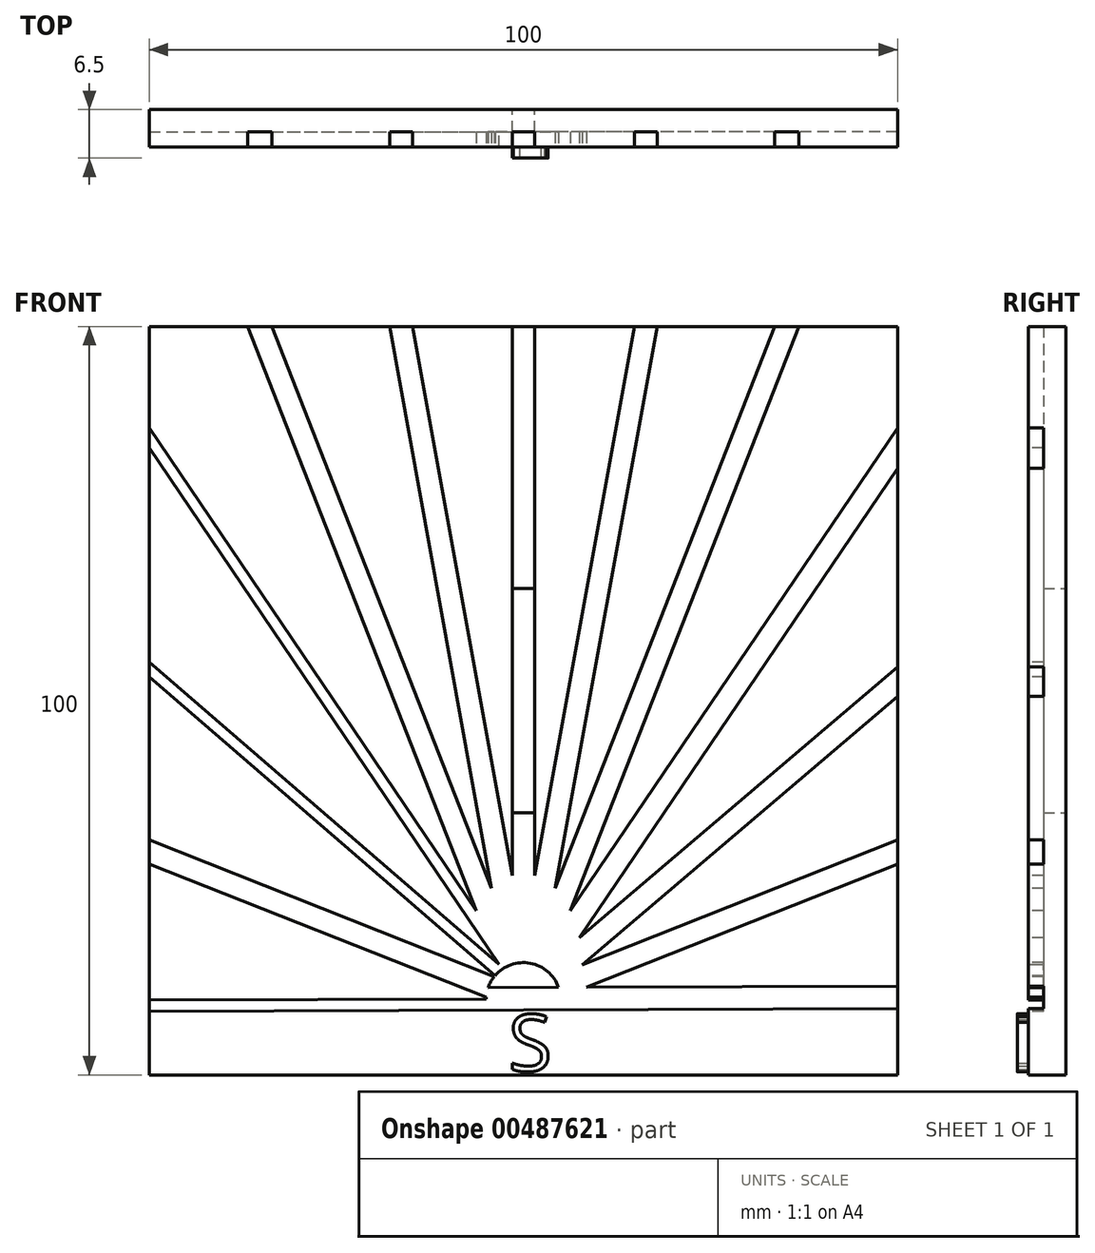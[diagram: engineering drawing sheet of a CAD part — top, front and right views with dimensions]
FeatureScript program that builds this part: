
annotation { "Feature Type Name" : "Feature", "Feature Type Description" : "" }
export const myFeature = defineFeature(function(context is Context, id is Id, definition is map)
    precondition{}
    {
        {
            var Q0;
            Q0=qCreatedBy(makeId("Front.planeOp"),FACE);
            var sketch = newSketch(context, id + "F0", { "sketchPlane" : qUnion([Q0])});
            skLineSegment(sketch, "E0.bottom", {"start": v(50, -50) * mm, "end": v(-50, -50) * mm});
            skLineSegment(sketch, "E0.top", {"start": v(50, 50) * mm, "end": v(-50, 50) * mm});
            skLineSegment(sketch, "E0.left", {"start": v(50, -50) * mm, "end": v(50, 50) * mm});
            skLineSegment(sketch, "E0.right", {"start": v(-50, -50) * mm, "end": v(-50, 50) * mm});
            skPoint(sketch, "E0.middle", {"position": v(0, 0) * mm});
            skLineSegment(sketch, "E1.bottom", {"start": v(1.5, -15) * mm, "end": v(-1.5, -15) * mm});
            skLineSegment(sketch, "E1.top", {"start": v(1.5, 15) * mm, "end": v(-1.5, 15) * mm});
            skLineSegment(sketch, "E1.left", {"start": v(1.5, -15) * mm, "end": v(1.5, 15) * mm});
            skLineSegment(sketch, "E1.right", {"start": v(-1.5, -15) * mm, "end": v(-1.5, 15) * mm});
            skSolve(sketch);
        }
        {
            var Q0;
            Q0=makeQuery(id+"F0.imprint","IMPRINT",FACE,{"disambiguationData":[TD([[makeQuery(id+"F0.imprint","IMPRINT",EDGE,{"derivedFrom":sQuery(id+"F0.wireOp",EDGE,"E0.bottom")}),-1.0]])]});
            extrude(context, id + "F1", {"entities" : qUnion([Q0]), "depth" : 5 * mm});
        }
        {
            var Q0;
            Q0=makeQuery(id+"F1.opExtrude","CAP_FACE",FACE,{"disambiguationData":[OSD([sQuery(id+"F0.wireOp",EDGE,"E0.bottom"),sQuery(id+"F0.wireOp",EDGE,"E0.top"),sQuery(id+"F0.wireOp",EDGE,"E0.left"),sQuery(id+"F0.wireOp",EDGE,"E0.right"),sQuery(id+"F0.wireOp",EDGE,"E1.bottom"),sQuery(id+"F0.wireOp",EDGE,"E1.top"),sQuery(id+"F0.wireOp",EDGE,"E1.left"),sQuery(id+"F0.wireOp",EDGE,"E1.right")])],"isStart":false});
            var sketch = newSketch(context, id + "F2", { "sketchPlane" : qUnion([Q0])});
            skPoint(sketch, "E2", {"position": v(0, -40) * mm});
            skLineSegment(sketch, "E3", {"start": v(-50, -40) * mm, "end": v(50, -40) * mm});
            skPoint(sketch, "E4", {"position": v(-50, -20.23) * mm});
            skLineSegment(sketch, "E5", {"start": v(0, -40) * mm, "end": v(-50, -20.23) * mm});
            skCircle(sketch, "E6", {"center": v(0, -40) * mm, "radius": 5 * mm});
            skPoint(sketch, "E7", {"position": v(-50, -18.62) * mm});
            skPoint(sketch, "E8", {"position": v(-50, -21.85) * mm});
            skLineSegment(sketch, "E9", {"start": v(-50, -21.85) * mm, "end": v(-4.99, -39.64) * mm});
            skLineSegment(sketch, "E10", {"start": v(-50, -18.62) * mm, "end": v(-3.88, -36.85) * mm});
            skSolve(sketch);
        }
        {
            var Q0;
            {var subQ5=sQuery(id+"F2.wireOp",EDGE,"E10");Q0=makeQuery(id+"F2.imprint","IMPRINT",FACE,{"disambiguationData":[TD([[makeQuery(id+"F2.imprint","IMPRINT",EDGE,{"derivedFrom":subQ5}),-1.0]])]});}
            var Q1;
            {var subQ5=sQuery(id+"F2.wireOp",EDGE,"E9");Q1=makeQuery(id+"F2.imprint","IMPRINT",FACE,{"disambiguationData":[TD([[makeQuery(id+"F2.imprint","IMPRINT",EDGE,{"derivedFrom":subQ5}),1.0]])]});}
            extrude(context, id + "F3", {"entities" : qUnion([Q0, Q1]), "operationType" : NewBodyOperationType.REMOVE, "oppositeDirection" : true, "depth" : 2 * mm});
        }
        {
            var Q0;
            Q0=makeQuery(id+"F1.opExtrude","CAP_FACE",FACE,{"disambiguationData":[OSD([sQuery(id+"F0.wireOp",EDGE,"E0.bottom"),sQuery(id+"F0.wireOp",EDGE,"E0.top"),sQuery(id+"F0.wireOp",EDGE,"E0.left"),sQuery(id+"F0.wireOp",EDGE,"E0.right"),sQuery(id+"F0.wireOp",EDGE,"E1.bottom"),sQuery(id+"F0.wireOp",EDGE,"E1.top"),sQuery(id+"F0.wireOp",EDGE,"E1.left"),sQuery(id+"F0.wireOp",EDGE,"E1.right")])],"isStart":false});
            var sketch = newSketch(context, id + "F4", { "sketchPlane" : qUnion([Q0])});
            skPoint(sketch, "E11", {"position": v(50, -41.82) * mm});
            skPoint(sketch, "E12", {"position": v(-50, 3.2) * mm});
            skPoint(sketch, "E13", {"position": v(0, -40) * mm});
            skCircle(sketch, "E14", {"center": v(0, -40) * mm, "radius": 5 * mm});
            skLineSegment(sketch, "E15", {"start": v(-50, 3.2) * mm, "end": v(0, -40) * mm});
            skLineSegment(sketch, "E16", {"start": v(0, -40) * mm, "end": v(-50, -39.64) * mm});
            skPoint(sketch, "E17", {"position": v(-50, 1.22) * mm});
            skPoint(sketch, "E18", {"position": v(-50, 5.19) * mm});
            skLineSegment(sketch, "E19", {"start": v(-50, 5.19) * mm, "end": v(-2.63, -35.75) * mm});
            skLineSegment(sketch, "E20", {"start": v(-50, 1.22) * mm, "end": v(-4.59, -38.02) * mm});
            skSolve(sketch);
        }
        {
            var Q0;
            {var subQ0=sQuery(id+"F4.wireOp",EDGE,"E19");Q0=makeQuery(id+"F4.imprint","IMPRINT",FACE,{"disambiguationData":[TD([[makeQuery(id+"F4.imprint","IMPRINT",EDGE,{"derivedFrom":subQ0}),-1.0]])]});}
            var Q1;
            {var subQ0=sQuery(id+"F4.wireOp",EDGE,"E14");var subQ1=sQuery(id+"F2.wireOp",EDGE,"E10");var subQ2=makeQuery(id+"F3.boolean.opBoolean","COPY",EDGE,{"derivedFrom":makeQuery(id+"F3.opExtrude","CAP_EDGE",EDGE,{"disambiguationData":[OSD([subQ1])],"isStart":true})});var subQ3=makeQuery(id+"F4.imprint","INTERSECT",VERTEX,{"derivedFrom":[subQ2,subQ0]});Q1=makeQuery(id+"F4.imprint","IMPRINT",FACE,{"disambiguationData":[TD([[makeQuery(id+"F4.imprint","IMPRINT",EDGE,{"disambiguationData":[TD([[subQ3,1.0]])],"derivedFrom":subQ0}),-1.0]])]});}
            extrude(context, id + "F5", {"entities" : qUnion([Q0, Q1]), "operationType" : NewBodyOperationType.REMOVE, "oppositeDirection" : true, "depth" : 2 * mm});
        }
        {
            var Q0;
            {var subQ0=sQuery(id+"F0.wireOp",EDGE,"E1.right");var subQ1=sQuery(id+"F0.wireOp",EDGE,"E1.left");var subQ2=sQuery(id+"F0.wireOp",EDGE,"E1.top");var subQ3=sQuery(id+"F0.wireOp",EDGE,"E1.bottom");var subQ4=sQuery(id+"F0.wireOp",EDGE,"E0.bottom");var subQ5=sQuery(id+"F0.wireOp",EDGE,"E0.right");var subQ6=sQuery(id+"F0.wireOp",EDGE,"E0.top");var subQ7=sQuery(id+"F0.wireOp",EDGE,"E0.left");Q0=makeQuery(id+"F5.boolean.opBoolean","SPLIT",FACE,{"disambiguationData":[TD([makeQuery(id+"F1.opExtrude","SWEPT_FACE",FACE,{"disambiguationData":[OSD([subQ4])]})])],"derivedFrom":makeQuery(id+"F1.opExtrude","CAP_FACE",FACE,{"disambiguationData":[OSD([subQ4,subQ6,subQ7,subQ5,subQ3,subQ2,subQ1,subQ0])],"isStart":false})});}
            var sketch = newSketch(context, id + "F6", { "sketchPlane" : qUnion([Q0])});
            skPoint(sketch, "E21", {"position": v(-50, 33.77) * mm});
            skPoint(sketch, "E22", {"position": v(0, -40) * mm});
            skCircle(sketch, "E23", {"center": v(0, -40) * mm, "radius": 5 * mm});
            skLineSegment(sketch, "E24", {"start": v(-50, 33.77) * mm, "end": v(0, -40) * mm});
            skLineSegment(sketch, "E25", {"start": v(0, -40) * mm, "end": v(-50, -40) * mm});
            skPoint(sketch, "E26", {"position": v(-50, 31.1) * mm});
            skPoint(sketch, "E27", {"position": v(-50, 36.44) * mm});
            skLineSegment(sketch, "E28", {"start": v(-50, 36.44) * mm, "end": v(-1.43, -35.21) * mm});
            skLineSegment(sketch, "E29", {"start": v(-50, 31.1) * mm, "end": v(-3.92, -36.9) * mm});
            skSolve(sketch);
        }
        {
            var Q0;
            {var subQ0=sQuery(id+"F6.wireOp",EDGE,"E28");Q0=makeQuery(id+"F6.imprint","IMPRINT",FACE,{"disambiguationData":[TD([[makeQuery(id+"F6.imprint","IMPRINT",EDGE,{"derivedFrom":subQ0}),-1.0]])]});}
            var Q1;
            {var subQ0=sQuery(id+"F6.wireOp",EDGE,"E23");var subQ1=sQuery(id+"F4.wireOp",EDGE,"E19");var subQ2=makeQuery(id+"F5.boolean.opBoolean","COPY",EDGE,{"derivedFrom":makeQuery(id+"F5.opExtrude","CAP_EDGE",EDGE,{"disambiguationData":[OSD([subQ1])],"isStart":true})});var subQ3=makeQuery(id+"F6.imprint","INTERSECT",VERTEX,{"derivedFrom":[subQ2,subQ0]});Q1=makeQuery(id+"F6.imprint","IMPRINT",FACE,{"disambiguationData":[TD([[makeQuery(id+"F6.imprint","IMPRINT",EDGE,{"disambiguationData":[TD([[subQ3,1.0]])],"derivedFrom":subQ0}),-1.0]])]});}
            var Q2;
            {var subQ6=sQuery(id+"F4.wireOp",EDGE,"E19");var subQ9=makeQuery(id+"F5.boolean.opBoolean","COPY",EDGE,{"derivedFrom":makeQuery(id+"F5.opExtrude","CAP_EDGE",EDGE,{"disambiguationData":[OSD([subQ6])],"isStart":true})});var subQ11=sQuery(id+"F6.wireOp",EDGE,"E29");var subQ12=makeQuery(id+"F6.imprint","INTERSECT",VERTEX,{"derivedFrom":[subQ9,subQ11]});Q2=makeQuery(id+"F6.imprint","IMPRINT",FACE,{"disambiguationData":[TD([[makeQuery(id+"F6.imprint","IMPRINT",EDGE,{"disambiguationData":[TD([[subQ12,-1.0]])],"derivedFrom":subQ9}),1.0]])]});}
            extrude(context, id + "F7", {"entities" : qUnion([Q0, Q1, Q2]), "operationType" : NewBodyOperationType.REMOVE, "oppositeDirection" : true, "depth" : 2 * mm});
        }
        {
            var Q0;
            {var subQ0=sQuery(id+"F0.wireOp",EDGE,"E1.right");var subQ2=sQuery(id+"F0.wireOp",EDGE,"E1.left");var subQ5=sQuery(id+"F0.wireOp",EDGE,"E1.top");var subQ7=sQuery(id+"F0.wireOp",EDGE,"E1.bottom");var subQ9=sQuery(id+"F0.wireOp",EDGE,"E0.bottom");var subQ10=makeQuery(id+"F1.opExtrude","SWEPT_FACE",FACE,{"disambiguationData":[OSD([subQ9])]});var subQ12=sQuery(id+"F0.wireOp",EDGE,"E0.right");var subQ14=sQuery(id+"F0.wireOp",EDGE,"E0.top");var subQ16=sQuery(id+"F0.wireOp",EDGE,"E0.left");Q0=makeQuery(id+"F7.boolean.opBoolean","SPLIT",FACE,{"disambiguationData":[TD([subQ10])],"derivedFrom":makeQuery(id+"F5.boolean.opBoolean","SPLIT",FACE,{"disambiguationData":[TD([subQ10])],"derivedFrom":makeQuery(id+"F1.opExtrude","CAP_FACE",FACE,{"disambiguationData":[OSD([subQ9,subQ14,subQ16,subQ12,subQ7,subQ5,subQ2,subQ0])],"isStart":false})})});}
            var sketch = newSketch(context, id + "F8", { "sketchPlane" : qUnion([Q0])});
            skPoint(sketch, "E30", {"position": v(0, -40) * mm});
            skPoint(sketch, "E31", {"position": v(-35.22, 50) * mm});
            skLineSegment(sketch, "E32", {"start": v(-35.22, 50) * mm, "end": v(0, -40) * mm});
            skLineSegment(sketch, "E33", {"start": v(0, -40) * mm, "end": v(-50, -40) * mm});
            skPoint(sketch, "E34", {"position": v(-36.83, 50) * mm});
            skPoint(sketch, "E35", {"position": v(-33.6, 50) * mm});
            skCircle(sketch, "E36", {"center": v(0, -40) * mm, "radius": 5 * mm});
            skLineSegment(sketch, "E37", {"start": v(-33.6, 50) * mm, "end": v(-0.34, -35.01) * mm});
            skLineSegment(sketch, "E38", {"start": v(-36.83, 50) * mm, "end": v(-3.13, -36.1) * mm});
            skSolve(sketch);
        }
        {
            var Q0;
            {var subQ0=sQuery(id+"F8.wireOp",EDGE,"E32");var subQ1=makeQuery(id+"F1.opExtrude","CAP_EDGE",EDGE,{"disambiguationData":[OSD([sQuery(id+"F0.wireOp",EDGE,"E0.top")])],"isStart":false});var subQ2=makeQuery(id+"F8.imprint","INTERSECT",VERTEX,{"derivedFrom":[subQ1,subQ0]});Q0=makeQuery(id+"F8.imprint","IMPRINT",FACE,{"disambiguationData":[TD([[makeQuery(id+"F8.imprint","IMPRINT",EDGE,{"disambiguationData":[TD([[subQ2,-1.0]])],"derivedFrom":subQ0}),-1.0]])]});}
            var Q1;
            {var subQ5=sQuery(id+"F8.wireOp",EDGE,"E37");Q1=makeQuery(id+"F8.imprint","IMPRINT",FACE,{"disambiguationData":[TD([[makeQuery(id+"F8.imprint","IMPRINT",EDGE,{"derivedFrom":subQ5}),-1.0]])]});}
            extrude(context, id + "F9", {"entities" : qUnion([Q0, Q1]), "operationType" : NewBodyOperationType.REMOVE, "oppositeDirection" : true, "depth" : 2 * mm});
        }
        {
            var Q0;
            {var subQ0=sQuery(id+"F0.wireOp",EDGE,"E1.right");var subQ2=sQuery(id+"F0.wireOp",EDGE,"E1.left");var subQ5=sQuery(id+"F0.wireOp",EDGE,"E1.top");var subQ8=sQuery(id+"F0.wireOp",EDGE,"E1.bottom");var subQ10=sQuery(id+"F0.wireOp",EDGE,"E0.bottom");var subQ11=makeQuery(id+"F1.opExtrude","SWEPT_FACE",FACE,{"disambiguationData":[OSD([subQ10])]});var subQ13=sQuery(id+"F0.wireOp",EDGE,"E0.right");var subQ15=sQuery(id+"F0.wireOp",EDGE,"E0.top");var subQ17=sQuery(id+"F0.wireOp",EDGE,"E0.left");Q0=makeQuery(id+"F9.boolean.opBoolean","SPLIT",FACE,{"disambiguationData":[TD([subQ11])],"derivedFrom":makeQuery(id+"F7.boolean.opBoolean","SPLIT",FACE,{"disambiguationData":[TD([subQ11])],"derivedFrom":makeQuery(id+"F5.boolean.opBoolean","SPLIT",FACE,{"disambiguationData":[TD([subQ11])],"derivedFrom":makeQuery(id+"F1.opExtrude","CAP_FACE",FACE,{"disambiguationData":[OSD([subQ10,subQ15,subQ17,subQ13,subQ8,subQ5,subQ2,subQ0])],"isStart":false})})})});}
            var sketch = newSketch(context, id + "F10", { "sketchPlane" : qUnion([Q0])});
            skPoint(sketch, "E39", {"position": v(0, -40) * mm});
            skPoint(sketch, "E40", {"position": v(-16.36, 50) * mm});
            skPoint(sketch, "E41", {"position": v(-14.83, 50) * mm});
            skPoint(sketch, "E42", {"position": v(-17.88, 50) * mm});
            skCircle(sketch, "E43", {"center": v(0, -40) * mm, "radius": 5 * mm});
            skLineSegment(sketch, "E44", {"start": v(-16.36, 50) * mm, "end": v(0, -40) * mm});
            skLineSegment(sketch, "E45", {"start": v(0, -40) * mm, "end": v(-50, -40) * mm});
            skLineSegment(sketch, "E46", {"start": v(-17.88, 50) * mm, "end": v(-2.33, -35.58) * mm});
            skLineSegment(sketch, "E47", {"start": v(-14.83, 50) * mm, "end": v(0.62, -35.04) * mm});
            skSolve(sketch);
        }
        {
            var Q0;
            {var subQ3=sQuery(id+"F8.wireOp",EDGE,"E37");var subQ6=makeQuery(id+"F9.boolean.opBoolean","COPY",EDGE,{"derivedFrom":makeQuery(id+"F9.opExtrude","CAP_EDGE",EDGE,{"disambiguationData":[OSD([subQ3])],"isStart":true})});var subQ8=sQuery(id+"F10.wireOp",EDGE,"E46");var subQ10=makeQuery(id+"F10.imprint","INTERSECT",VERTEX,{"derivedFrom":[subQ6,subQ8]});Q0=makeQuery(id+"F10.imprint","IMPRINT",FACE,{"disambiguationData":[TD([[makeQuery(id+"F10.imprint","IMPRINT",EDGE,{"disambiguationData":[TD([[subQ10,-1.0]])],"derivedFrom":subQ6}),1.0]])]});}
            var Q1;
            {var subQ6=sQuery(id+"F10.wireOp",EDGE,"E47");Q1=makeQuery(id+"F10.imprint","IMPRINT",FACE,{"disambiguationData":[TD([[makeQuery(id+"F10.imprint","IMPRINT",EDGE,{"derivedFrom":subQ6}),-1.0]])]});}
            extrude(context, id + "F11", {"entities" : qUnion([Q0, Q1]), "operationType" : NewBodyOperationType.REMOVE, "oppositeDirection" : true, "depth" : 2 * mm});
        }
        {
            var Q0;
            {var subQ0=sQuery(id+"F0.wireOp",EDGE,"E1.right");var subQ2=sQuery(id+"F0.wireOp",EDGE,"E1.left");var subQ5=sQuery(id+"F0.wireOp",EDGE,"E1.top");var subQ8=sQuery(id+"F0.wireOp",EDGE,"E1.bottom");var subQ10=sQuery(id+"F0.wireOp",EDGE,"E0.bottom");var subQ11=makeQuery(id+"F1.opExtrude","SWEPT_FACE",FACE,{"disambiguationData":[OSD([subQ10])]});var subQ13=sQuery(id+"F0.wireOp",EDGE,"E0.right");var subQ15=sQuery(id+"F0.wireOp",EDGE,"E0.top");var subQ17=sQuery(id+"F0.wireOp",EDGE,"E0.left");Q0=makeQuery(id+"F11.boolean.opBoolean","SPLIT",FACE,{"disambiguationData":[TD([subQ11])],"derivedFrom":makeQuery(id+"F9.boolean.opBoolean","SPLIT",FACE,{"disambiguationData":[TD([subQ11])],"derivedFrom":makeQuery(id+"F7.boolean.opBoolean","SPLIT",FACE,{"disambiguationData":[TD([subQ11])],"derivedFrom":makeQuery(id+"F5.boolean.opBoolean","SPLIT",FACE,{"disambiguationData":[TD([subQ11])],"derivedFrom":makeQuery(id+"F1.opExtrude","CAP_FACE",FACE,{"disambiguationData":[OSD([subQ10,subQ15,subQ17,subQ13,subQ8,subQ5,subQ2,subQ0])],"isStart":false})})})})});}
            var sketch = newSketch(context, id + "F12", { "sketchPlane" : qUnion([Q0])});
            skPoint(sketch, "E48", {"position": v(0, -40) * mm});
            skPoint(sketch, "E49", {"position": v(0, 50) * mm});
            skLineSegment(sketch, "E50", {"start": v(0, 50) * mm, "end": v(0, -40) * mm});
            skPoint(sketch, "E51", {"position": v(-1.5, 50) * mm});
            skPoint(sketch, "E52", {"position": v(1.5, 50) * mm});
            skCircle(sketch, "E53", {"center": v(0, -40) * mm, "radius": 5 * mm});
            skLineSegment(sketch, "E54", {"start": v(-1.5, 50) * mm, "end": v(-1.5, -35.23) * mm});
            skLineSegment(sketch, "E55", {"start": v(1.5, 50) * mm, "end": v(1.5, -35.23) * mm});
            skSolve(sketch);
        }
        {
            var Q0;
            {var subQ0=sQuery(id+"F12.wireOp",EDGE,"E50");var subQ1=sQuery(id+"F0.wireOp",EDGE,"E1.top");var subQ9=makeQuery(id+"F1.opExtrude","CAP_EDGE",EDGE,{"disambiguationData":[OSD([subQ1])],"isStart":false});var subQ10=makeQuery(id+"F12.imprint","INTERSECT",VERTEX,{"derivedFrom":[subQ9,subQ0]});Q0=makeQuery(id+"F12.imprint","IMPRINT",FACE,{"disambiguationData":[TD([[makeQuery(id+"F12.imprint","IMPRINT",EDGE,{"disambiguationData":[TD([[subQ10,-1.0]])],"derivedFrom":subQ9}),-1.0]])]});}
            var Q1;
            {var subQ0=sQuery(id+"F12.wireOp",EDGE,"E50");var subQ1=sQuery(id+"F0.wireOp",EDGE,"E1.top");var subQ9=makeQuery(id+"F1.opExtrude","CAP_EDGE",EDGE,{"disambiguationData":[OSD([subQ1])],"isStart":false});var subQ10=makeQuery(id+"F12.imprint","INTERSECT",VERTEX,{"derivedFrom":[subQ9,subQ0]});Q1=makeQuery(id+"F12.imprint","IMPRINT",FACE,{"disambiguationData":[TD([[makeQuery(id+"F12.imprint","IMPRINT",EDGE,{"disambiguationData":[TD([[subQ10,1.0]])],"derivedFrom":subQ9}),-1.0]])]});}
            var Q2;
            {var subQ0=sQuery(id+"F12.wireOp",EDGE,"E50");var subQ1=makeQuery(id+"F1.opExtrude","CAP_EDGE",EDGE,{"disambiguationData":[OSD([sQuery(id+"F0.wireOp",EDGE,"E1.bottom")])],"isStart":false});var subQ2=makeQuery(id+"F12.imprint","INTERSECT",VERTEX,{"derivedFrom":[subQ1,subQ0]});Q2=makeQuery(id+"F12.imprint","IMPRINT",FACE,{"disambiguationData":[TD([[makeQuery(id+"F12.imprint","IMPRINT",EDGE,{"disambiguationData":[TD([[subQ2,-1.0]])],"derivedFrom":subQ0}),-1.0]])]});}
            var Q3;
            {var subQ3=makeQuery(id+"F1.opExtrude","CAP_EDGE",EDGE,{"disambiguationData":[OSD([sQuery(id+"F0.wireOp",EDGE,"E1.bottom")])],"isStart":false});var subQ7=sQuery(id+"F12.wireOp",EDGE,"E50");var subQ9=makeQuery(id+"F12.imprint","INTERSECT",VERTEX,{"derivedFrom":[subQ3,subQ7]});Q3=makeQuery(id+"F12.imprint","IMPRINT",FACE,{"disambiguationData":[TD([[makeQuery(id+"F12.imprint","IMPRINT",EDGE,{"disambiguationData":[TD([[subQ9,-1.0]])],"derivedFrom":subQ7}),1.0]])]});}
            var Q4;
            {var subQ0=sQuery(id+"F12.wireOp",EDGE,"E53");var subQ1=sQuery(id+"F12.wireOp",EDGE,"E50");var subQ2=makeQuery(id+"F12.imprint","INTERSECT",VERTEX,{"derivedFrom":[subQ1,subQ0]});Q4=makeQuery(id+"F12.imprint","IMPRINT",FACE,{"disambiguationData":[TD([[makeQuery(id+"F12.imprint","IMPRINT",EDGE,{"disambiguationData":[TD([[subQ2,1.0]])],"derivedFrom":subQ1}),-1.0]])]});}
            extrude(context, id + "F13", {"entities" : qUnion([Q0, Q1, Q2, Q3, Q4]), "operationType" : NewBodyOperationType.REMOVE, "oppositeDirection" : true, "depth" : 2 * mm});
        }
        {
            var Q0;
            {var subQ0=sQuery(id+"F0.wireOp",EDGE,"E1.left");var subQ3=sQuery(id+"F0.wireOp",EDGE,"E1.top");var subQ7=sQuery(id+"F0.wireOp",EDGE,"E1.bottom");var subQ9=sQuery(id+"F0.wireOp",EDGE,"E0.bottom");var subQ10=makeQuery(id+"F1.opExtrude","SWEPT_FACE",FACE,{"disambiguationData":[OSD([subQ9])]});var subQ12=sQuery(id+"F0.wireOp",EDGE,"E0.right");var subQ14=sQuery(id+"F0.wireOp",EDGE,"E0.top");var subQ20=sQuery(id+"F0.wireOp",EDGE,"E0.left");var subQ24=sQuery(id+"F0.wireOp",EDGE,"E1.right");var subQ25=makeQuery(id+"F1.opExtrude","CAP_FACE",FACE,{"disambiguationData":[OSD([subQ9,subQ14,subQ20,subQ12,subQ7,subQ3,subQ0,subQ24])],"isStart":false});Q0=makeQuery(id+"F13.boolean.opBoolean","SPLIT",FACE,{"disambiguationData":[TD([subQ10])],"derivedFrom":makeQuery(id+"F11.boolean.opBoolean","SPLIT",FACE,{"disambiguationData":[TD([subQ10])],"derivedFrom":makeQuery(id+"F9.boolean.opBoolean","SPLIT",FACE,{"disambiguationData":[TD([subQ10])],"derivedFrom":makeQuery(id+"F7.boolean.opBoolean","SPLIT",FACE,{"disambiguationData":[TD([subQ10])],"derivedFrom":makeQuery(id+"F5.boolean.opBoolean","SPLIT",FACE,{"disambiguationData":[TD([subQ10])],"derivedFrom":subQ25})})})})});}
            var sketch = newSketch(context, id + "F14", { "sketchPlane" : qUnion([Q0])});
            skPoint(sketch, "E56", {"position": v(16.36, 50) * mm});
            skPoint(sketch, "E57", {"position": v(0, -40) * mm});
            skCircle(sketch, "E58", {"center": v(0, -40) * mm, "radius": 5 * mm});
            skLineSegment(sketch, "E59", {"start": v(16.36, 50) * mm, "end": v(0, -40) * mm});
            skLineSegment(sketch, "E60", {"start": v(0, -40) * mm, "end": v(50, -40) * mm});
            skPoint(sketch, "E61", {"position": v(14.83, 50) * mm});
            skPoint(sketch, "E62", {"position": v(17.88, 50) * mm});
            skLineSegment(sketch, "E63", {"start": v(17.88, 50) * mm, "end": v(2.33, -35.58) * mm});
            skLineSegment(sketch, "E64", {"start": v(14.83, 50) * mm, "end": v(-0.62, -35.04) * mm});
            skSolve(sketch);
        }
        {
            var Q0;
            {var subQ7=sQuery(id+"F14.wireOp",EDGE,"E63");Q0=makeQuery(id+"F14.imprint","IMPRINT",FACE,{"disambiguationData":[TD([[makeQuery(id+"F14.imprint","IMPRINT",EDGE,{"derivedFrom":subQ7}),-1.0]])]});}
            var Q1;
            {var subQ6=sQuery(id+"F12.wireOp",EDGE,"E55");var subQ12=makeQuery(id+"F13.boolean.opBoolean","COPY",EDGE,{"derivedFrom":makeQuery(id+"F13.opExtrude","CAP_EDGE",EDGE,{"disambiguationData":[OSD([subQ6]),TDD([makeQuery(id+"F12.imprint","IMPRINT",EDGE,{"disambiguationData":[TD([[makeQuery(id+"F12.imprint","INTERSECT",VERTEX,{"derivedFrom":[sQuery(id+"F12.wireOp",EDGE,"E53"),subQ6]}),1.0]])],"derivedFrom":subQ6})])],"isStart":true})});var subQ14=sQuery(id+"F14.wireOp",EDGE,"U3o0jyPI-7KGk-aDnc-HRvP-a0akFUZvhtuf");var subQ16=makeQuery(id+"F14.imprint","INTERSECT",VERTEX,{"derivedFrom":[subQ12,subQ14]});Q1=makeQuery(id+"F14.imprint","IMPRINT",FACE,{"disambiguationData":[TD([[makeQuery(id+"F14.imprint","IMPRINT",EDGE,{"disambiguationData":[TD([[subQ16,-1.0]])],"derivedFrom":subQ12}),1.0]])]});}
            var Q2;
            {var subQ1=sQuery(id+"F0.wireOp",EDGE,"E0.left");var subQ2=makeQuery(id+"F1.opExtrude","SWEPT_FACE",FACE,{"disambiguationData":[OSD([subQ1])]});var subQ3=sQuery(id+"F0.wireOp",EDGE,"E1.left");var subQ4=sQuery(id+"F0.wireOp",EDGE,"E0.top");var subQ6=sQuery(id+"F12.wireOp",EDGE,"E55");var subQ7=sQuery(id+"F0.wireOp",EDGE,"E1.bottom");var subQ8=makeQuery(id+"F12.imprint","IMPRINT",EDGE,{"disambiguationData":[TD([[makeQuery(id+"F12.imprint","INTERSECT",VERTEX,{"derivedFrom":[makeQuery(id+"F1.opExtrude","CAP_EDGE",EDGE,{"disambiguationData":[OSD([subQ7])],"isStart":false}),subQ6]}),-1.0],[makeQuery(id+"F12.imprint","INTERSECT",VERTEX,{"derivedFrom":[sQuery(id+"F12.wireOp",EDGE,"E53"),subQ6]}),1.0]])],"derivedFrom":subQ6});var subQ9=sQuery(id+"F0.wireOp",EDGE,"E1.top");var subQ11=makeQuery(id+"F11.boolean.opBoolean","SPLIT",EDGE,{"disambiguationData":[TD([subQ2])],"derivedFrom":makeQuery(id+"F9.boolean.opBoolean","SPLIT",EDGE,{"disambiguationData":[TD([subQ2])],"derivedFrom":makeQuery(id+"F1.opExtrude","CAP_EDGE",EDGE,{"disambiguationData":[OSD([subQ4])],"isStart":false})})});var subQ12=makeQuery(id+"F12.imprint","IMPRINT",EDGE,{"disambiguationData":[TD([[makeQuery(id+"F12.imprint","INTERSECT",VERTEX,{"derivedFrom":[makeQuery(id+"F1.opExtrude","CAP_EDGE",EDGE,{"disambiguationData":[OSD([subQ9])],"isStart":false}),subQ6]}),1.0],[makeQuery(id+"F12.imprint","INTERSECT",VERTEX,{"derivedFrom":[subQ11,subQ6]}),-1.0]])],"derivedFrom":subQ6});var subQ15=makeQuery(id+"F13.boolean.opBoolean","MERGE",EDGE,{"derivedFrom":[makeQuery(id+"F1.opExtrude","CAP_EDGE",EDGE,{"disambiguationData":[OSD([subQ3])],"isStart":false}),makeQuery(id+"F13.opExtrude","CAP_EDGE",EDGE,{"disambiguationData":[OSD([subQ6]),TDD([subQ12])],"isStart":true}),makeQuery(id+"F13.opExtrude","CAP_EDGE",EDGE,{"disambiguationData":[OSD([subQ6]),TDD([subQ8])],"isStart":true})]});var subQ17=sQuery(id+"F14.wireOp",EDGE,"E64");var subQ18=makeQuery(id+"F14.imprint","INTERSECT",VERTEX,{"derivedFrom":[subQ15,subQ17]});Q2=makeQuery(id+"F14.imprint","IMPRINT",FACE,{"disambiguationData":[TD([[makeQuery(id+"F14.imprint","IMPRINT",EDGE,{"disambiguationData":[TD([[subQ18,1.0]])],"derivedFrom":subQ15}),-1.0]])]});}
            extrude(context, id + "F15", {"entities" : qUnion([Q0, Q1, Q2]), "operationType" : NewBodyOperationType.REMOVE, "oppositeDirection" : true, "depth" : 2 * mm});
        }
        {
            var Q0;
            {var subQ4=sQuery(id+"F0.wireOp",EDGE,"E0.bottom");var subQ5=makeQuery(id+"F1.opExtrude","SWEPT_FACE",FACE,{"disambiguationData":[OSD([subQ4])]});var subQ8=sQuery(id+"F0.wireOp",EDGE,"E0.right");var subQ10=sQuery(id+"F0.wireOp",EDGE,"E0.top");var subQ17=sQuery(id+"F0.wireOp",EDGE,"E0.left");var subQ19=sQuery(id+"F0.wireOp",EDGE,"E1.left");var subQ21=sQuery(id+"F0.wireOp",EDGE,"E1.top");var subQ23=sQuery(id+"F0.wireOp",EDGE,"E1.bottom");var subQ25=sQuery(id+"F0.wireOp",EDGE,"E1.right");var subQ26=makeQuery(id+"F1.opExtrude","CAP_FACE",FACE,{"disambiguationData":[OSD([subQ4,subQ10,subQ17,subQ8,subQ23,subQ21,subQ19,subQ25])],"isStart":false});Q0=makeQuery(id+"F15.boolean.opBoolean","SPLIT",FACE,{"disambiguationData":[TD([subQ5])],"derivedFrom":makeQuery(id+"F13.boolean.opBoolean","SPLIT",FACE,{"disambiguationData":[TD([subQ5])],"derivedFrom":makeQuery(id+"F11.boolean.opBoolean","SPLIT",FACE,{"disambiguationData":[TD([subQ5])],"derivedFrom":makeQuery(id+"F9.boolean.opBoolean","SPLIT",FACE,{"disambiguationData":[TD([subQ5])],"derivedFrom":makeQuery(id+"F7.boolean.opBoolean","SPLIT",FACE,{"disambiguationData":[TD([subQ5])],"derivedFrom":makeQuery(id+"F5.boolean.opBoolean","SPLIT",FACE,{"disambiguationData":[TD([subQ5])],"derivedFrom":subQ26})})})})})});}
            var sketch = newSketch(context, id + "F16", { "sketchPlane" : qUnion([Q0])});
            skPoint(sketch, "E65", {"position": v(35.22, 50) * mm});
            skPoint(sketch, "E66", {"position": v(0, -40) * mm});
            skPoint(sketch, "E67", {"position": v(33.6, 50) * mm});
            skPoint(sketch, "E68", {"position": v(36.83, 50) * mm});
            skCircle(sketch, "E69", {"center": v(0, -40) * mm, "radius": 5 * mm});
            skLineSegment(sketch, "E70", {"start": v(35.22, 50) * mm, "end": v(0, -40) * mm});
            skLineSegment(sketch, "E71", {"start": v(0, -40) * mm, "end": v(50, -40) * mm});
            skLineSegment(sketch, "E72", {"start": v(36.83, 50) * mm, "end": v(3.13, -36.1) * mm});
            skLineSegment(sketch, "E73", {"start": v(33.6, 50) * mm, "end": v(0.34, -35.01) * mm});
            skSolve(sketch);
        }
        {
            var Q0;
            {var subQ7=sQuery(id+"F14.wireOp",EDGE,"E63");var subQ12=makeQuery(id+"F15.boolean.opBoolean","COPY",EDGE,{"derivedFrom":makeQuery(id+"F15.opExtrude","CAP_EDGE",EDGE,{"disambiguationData":[OSD([subQ7])],"isStart":true})});var subQ14=sQuery(id+"F16.wireOp",EDGE,"E73");var subQ15=makeQuery(id+"F16.imprint","INTERSECT",VERTEX,{"derivedFrom":[subQ12,subQ14]});Q0=makeQuery(id+"F16.imprint","IMPRINT",FACE,{"disambiguationData":[TD([[makeQuery(id+"F16.imprint","IMPRINT",EDGE,{"disambiguationData":[TD([[subQ15,-1.0]])],"derivedFrom":subQ12}),1.0]])]});}
            var Q1;
            {var subQ6=sQuery(id+"F16.wireOp",EDGE,"E72");Q1=makeQuery(id+"F16.imprint","IMPRINT",FACE,{"disambiguationData":[TD([[makeQuery(id+"F16.imprint","IMPRINT",EDGE,{"derivedFrom":subQ6}),-1.0]])]});}
            extrude(context, id + "F17", {"entities" : qUnion([Q0, Q1]), "operationType" : NewBodyOperationType.REMOVE, "oppositeDirection" : true, "depth" : 2 * mm});
        }
        {
            var Q0;
            {var subQ4=sQuery(id+"F0.wireOp",EDGE,"E0.bottom");var subQ5=makeQuery(id+"F1.opExtrude","SWEPT_FACE",FACE,{"disambiguationData":[OSD([subQ4])]});var subQ9=sQuery(id+"F0.wireOp",EDGE,"E0.right");var subQ11=sQuery(id+"F0.wireOp",EDGE,"E0.top");var subQ18=sQuery(id+"F0.wireOp",EDGE,"E0.left");var subQ20=sQuery(id+"F0.wireOp",EDGE,"E1.left");var subQ22=sQuery(id+"F0.wireOp",EDGE,"E1.bottom");var subQ23=sQuery(id+"F0.wireOp",EDGE,"E1.top");var subQ24=sQuery(id+"F0.wireOp",EDGE,"E1.right");var subQ25=makeQuery(id+"F1.opExtrude","CAP_FACE",FACE,{"disambiguationData":[OSD([subQ4,subQ11,subQ18,subQ9,subQ22,subQ23,subQ20,subQ24])],"isStart":false});Q0=makeQuery(id+"F17.boolean.opBoolean","SPLIT",FACE,{"disambiguationData":[TD([subQ5])],"derivedFrom":makeQuery(id+"F15.boolean.opBoolean","SPLIT",FACE,{"disambiguationData":[TD([subQ5])],"derivedFrom":makeQuery(id+"F13.boolean.opBoolean","SPLIT",FACE,{"disambiguationData":[TD([subQ5])],"derivedFrom":makeQuery(id+"F11.boolean.opBoolean","SPLIT",FACE,{"disambiguationData":[TD([subQ5])],"derivedFrom":makeQuery(id+"F9.boolean.opBoolean","SPLIT",FACE,{"disambiguationData":[TD([subQ5])],"derivedFrom":makeQuery(id+"F7.boolean.opBoolean","SPLIT",FACE,{"disambiguationData":[TD([subQ5])],"derivedFrom":makeQuery(id+"F5.boolean.opBoolean","SPLIT",FACE,{"disambiguationData":[TD([subQ5])],"derivedFrom":subQ25})})})})})})});}
            var sketch = newSketch(context, id + "F18", { "sketchPlane" : qUnion([Q0])});
            skPoint(sketch, "E74", {"position": v(50, 33.77) * mm});
            skPoint(sketch, "E75", {"position": v(50, 36.44) * mm});
            skPoint(sketch, "E76", {"position": v(50, 31.1) * mm});
            skPoint(sketch, "E77", {"position": v(0, -40) * mm});
            skLineSegment(sketch, "E78", {"start": v(50, 33.77) * mm, "end": v(0, -40) * mm});
            skLineSegment(sketch, "E79", {"start": v(0, -40) * mm, "end": v(50, -40) * mm});
            skCircle(sketch, "E80", {"center": v(0, -40) * mm, "radius": 5 * mm});
            skLineSegment(sketch, "E81", {"start": v(50, 36.44) * mm, "end": v(1.43, -35.21) * mm});
            skLineSegment(sketch, "E82", {"start": v(50, 31.1) * mm, "end": v(3.92, -36.9) * mm});
            skSolve(sketch);
        }
        {
            var Q0;
            {var subQ0=sQuery(id+"F18.wireOp",EDGE,"E78");var subQ1=makeQuery(id+"F1.opExtrude","CAP_EDGE",EDGE,{"disambiguationData":[OSD([sQuery(id+"F0.wireOp",EDGE,"E0.left")])],"isStart":false});var subQ2=makeQuery(id+"F18.imprint","INTERSECT",VERTEX,{"derivedFrom":[subQ1,subQ0]});Q0=makeQuery(id+"F18.imprint","IMPRINT",FACE,{"disambiguationData":[TD([[makeQuery(id+"F18.imprint","IMPRINT",EDGE,{"disambiguationData":[TD([[subQ2,-1.0]])],"derivedFrom":subQ0}),-1.0]])]});}
            var Q1;
            {var subQ0=sQuery(id+"F18.wireOp",EDGE,"E82");Q1=makeQuery(id+"F18.imprint","IMPRINT",FACE,{"disambiguationData":[TD([[makeQuery(id+"F18.imprint","IMPRINT",EDGE,{"derivedFrom":subQ0}),-1.0]])]});}
            extrude(context, id + "F19", {"entities" : qUnion([Q0, Q1]), "operationType" : NewBodyOperationType.REMOVE, "oppositeDirection" : true, "depth" : 2 * mm});
        }
        {
            var Q0;
            {var subQ10=sQuery(id+"F0.wireOp",EDGE,"E0.bottom");var subQ11=makeQuery(id+"F1.opExtrude","SWEPT_FACE",FACE,{"disambiguationData":[OSD([subQ10])]});var subQ12=sQuery(id+"F0.wireOp",EDGE,"E0.left");var subQ15=sQuery(id+"F0.wireOp",EDGE,"E0.right");var subQ19=sQuery(id+"F0.wireOp",EDGE,"E0.top");var subQ21=sQuery(id+"F0.wireOp",EDGE,"E1.left");var subQ23=sQuery(id+"F0.wireOp",EDGE,"E1.bottom");var subQ24=sQuery(id+"F0.wireOp",EDGE,"E1.top");var subQ25=sQuery(id+"F0.wireOp",EDGE,"E1.right");var subQ26=makeQuery(id+"F1.opExtrude","CAP_FACE",FACE,{"disambiguationData":[OSD([subQ10,subQ19,subQ12,subQ15,subQ23,subQ24,subQ21,subQ25])],"isStart":false});Q0=makeQuery(id+"F19.boolean.opBoolean","SPLIT",FACE,{"disambiguationData":[TD([subQ11])],"derivedFrom":makeQuery(id+"F17.boolean.opBoolean","SPLIT",FACE,{"disambiguationData":[TD([subQ11])],"derivedFrom":makeQuery(id+"F15.boolean.opBoolean","SPLIT",FACE,{"disambiguationData":[TD([subQ11])],"derivedFrom":makeQuery(id+"F13.boolean.opBoolean","SPLIT",FACE,{"disambiguationData":[TD([subQ11])],"derivedFrom":makeQuery(id+"F11.boolean.opBoolean","SPLIT",FACE,{"disambiguationData":[TD([subQ11])],"derivedFrom":makeQuery(id+"F9.boolean.opBoolean","SPLIT",FACE,{"disambiguationData":[TD([subQ11])],"derivedFrom":makeQuery(id+"F7.boolean.opBoolean","SPLIT",FACE,{"disambiguationData":[TD([subQ11])],"derivedFrom":makeQuery(id+"F5.boolean.opBoolean","SPLIT",FACE,{"disambiguationData":[TD([subQ11])],"derivedFrom":subQ26})})})})})})})});}
            var sketch = newSketch(context, id + "F20", { "sketchPlane" : qUnion([Q0])});
            skPoint(sketch, "E83", {"position": v(50, 2.58) * mm});
            skPoint(sketch, "E84", {"position": v(50, 4.55) * mm});
            skPoint(sketch, "E85", {"position": v(0, -40) * mm});
            skLineSegment(sketch, "E86", {"start": v(50, 2.58) * mm, "end": v(0, -40) * mm});
            skLineSegment(sketch, "E87", {"start": v(0, -40) * mm, "end": v(50, -40) * mm});
            skPoint(sketch, "E88", {"position": v(50, 0.61) * mm});
            skCircle(sketch, "E89", {"center": v(0, -40) * mm, "radius": 5 * mm});
            skLineSegment(sketch, "E90", {"start": v(50, 4.55) * mm, "end": v(2.66, -35.77) * mm});
            skLineSegment(sketch, "E91", {"start": v(50, 0.61) * mm, "end": v(4.6, -38.05) * mm});
            skSolve(sketch);
        }
        {
            var Q0;
            {var subQ3=sQuery(id+"F18.wireOp",EDGE,"E82");var subQ6=makeQuery(id+"F19.boolean.opBoolean","COPY",EDGE,{"derivedFrom":makeQuery(id+"F19.opExtrude","CAP_EDGE",EDGE,{"disambiguationData":[OSD([subQ3])],"isStart":true})});var subQ8=sQuery(id+"F20.wireOp",EDGE,"E90");var subQ10=makeQuery(id+"F20.imprint","INTERSECT",VERTEX,{"derivedFrom":[subQ6,subQ8]});Q0=makeQuery(id+"F20.imprint","IMPRINT",FACE,{"disambiguationData":[TD([[makeQuery(id+"F20.imprint","IMPRINT",EDGE,{"disambiguationData":[TD([[subQ10,-1.0]])],"derivedFrom":subQ6}),1.0]])]});}
            var Q1;
            {var subQ6=sQuery(id+"F20.wireOp",EDGE,"E91");Q1=makeQuery(id+"F20.imprint","IMPRINT",FACE,{"disambiguationData":[TD([[makeQuery(id+"F20.imprint","IMPRINT",EDGE,{"derivedFrom":subQ6}),-1.0]])]});}
            extrude(context, id + "F21", {"entities" : qUnion([Q0, Q1]), "operationType" : NewBodyOperationType.REMOVE, "oppositeDirection" : true, "depth" : 2 * mm});
        }
        {
            var Q0;
            {var subQ10=sQuery(id+"F0.wireOp",EDGE,"E0.bottom");var subQ11=makeQuery(id+"F1.opExtrude","SWEPT_FACE",FACE,{"disambiguationData":[OSD([subQ10])]});var subQ12=sQuery(id+"F0.wireOp",EDGE,"E0.left");var subQ15=sQuery(id+"F0.wireOp",EDGE,"E0.right");var subQ20=sQuery(id+"F0.wireOp",EDGE,"E0.top");var subQ22=sQuery(id+"F0.wireOp",EDGE,"E1.left");var subQ24=sQuery(id+"F0.wireOp",EDGE,"E1.bottom");var subQ25=sQuery(id+"F0.wireOp",EDGE,"E1.top");var subQ26=sQuery(id+"F0.wireOp",EDGE,"E1.right");var subQ27=makeQuery(id+"F1.opExtrude","CAP_FACE",FACE,{"disambiguationData":[OSD([subQ10,subQ20,subQ12,subQ15,subQ24,subQ25,subQ22,subQ26])],"isStart":false});Q0=makeQuery(id+"F21.boolean.opBoolean","SPLIT",FACE,{"disambiguationData":[TD([subQ11])],"derivedFrom":makeQuery(id+"F19.boolean.opBoolean","SPLIT",FACE,{"disambiguationData":[TD([subQ11])],"derivedFrom":makeQuery(id+"F17.boolean.opBoolean","SPLIT",FACE,{"disambiguationData":[TD([subQ11])],"derivedFrom":makeQuery(id+"F15.boolean.opBoolean","SPLIT",FACE,{"disambiguationData":[TD([subQ11])],"derivedFrom":makeQuery(id+"F13.boolean.opBoolean","SPLIT",FACE,{"disambiguationData":[TD([subQ11])],"derivedFrom":makeQuery(id+"F11.boolean.opBoolean","SPLIT",FACE,{"disambiguationData":[TD([subQ11])],"derivedFrom":makeQuery(id+"F9.boolean.opBoolean","SPLIT",FACE,{"disambiguationData":[TD([subQ11])],"derivedFrom":makeQuery(id+"F7.boolean.opBoolean","SPLIT",FACE,{"disambiguationData":[TD([subQ11])],"derivedFrom":makeQuery(id+"F5.boolean.opBoolean","SPLIT",FACE,{"disambiguationData":[TD([subQ11])],"derivedFrom":subQ27})})})})})})})})});}
            var sketch = newSketch(context, id + "F22", { "sketchPlane" : qUnion([Q0])});
            skPoint(sketch, "E92", {"position": v(50, -20.23) * mm});
            skPoint(sketch, "E93", {"position": v(50, -18.62) * mm});
            skPoint(sketch, "E94", {"position": v(50, -21.85) * mm});
            skPoint(sketch, "E95", {"position": v(0, -40) * mm});
            skLineSegment(sketch, "E96", {"start": v(50, -20.23) * mm, "end": v(0, -40) * mm});
            skCircle(sketch, "E97", {"center": v(0, -40) * mm, "radius": 5 * mm});
            skLineSegment(sketch, "E98", {"start": v(50, -18.62) * mm, "end": v(3.88, -36.85) * mm});
            skLineSegment(sketch, "E99", {"start": v(50, -21.85) * mm, "end": v(4.99, -39.64) * mm});
            skLineSegment(sketch, "E100", {"start": v(0, -40) * mm, "end": v(50, -40) * mm});
            skSolve(sketch);
        }
        {
            var Q0;
            {var subQ10=sQuery(id+"F22.wireOp",EDGE,"E99");Q0=makeQuery(id+"F22.imprint","IMPRINT",FACE,{"disambiguationData":[TD([[makeQuery(id+"F22.imprint","IMPRINT",EDGE,{"derivedFrom":subQ10}),-1.0]])]});}
            var Q1;
            {var subQ0=sQuery(id+"F22.wireOp",EDGE,"E97");var subQ1=sQuery(id+"F20.wireOp",EDGE,"E91");var subQ2=makeQuery(id+"F21.boolean.opBoolean","COPY",EDGE,{"derivedFrom":makeQuery(id+"F21.opExtrude","CAP_EDGE",EDGE,{"disambiguationData":[OSD([subQ1])],"isStart":true})});var subQ3=makeQuery(id+"F22.imprint","INTERSECT",VERTEX,{"derivedFrom":[subQ2,subQ0]});Q1=makeQuery(id+"F22.imprint","IMPRINT",FACE,{"disambiguationData":[TD([[makeQuery(id+"F22.imprint","IMPRINT",EDGE,{"disambiguationData":[TD([[subQ3,1.0]])],"derivedFrom":subQ0}),-1.0]])]});}
            extrude(context, id + "F23", {"entities" : qUnion([Q0, Q1]), "operationType" : NewBodyOperationType.REMOVE, "oppositeDirection" : true, "depth" : 2 * mm});
        }
        {
            var Q0;
            {var subQ10=sQuery(id+"F0.wireOp",EDGE,"E0.bottom");var subQ11=makeQuery(id+"F1.opExtrude","SWEPT_FACE",FACE,{"disambiguationData":[OSD([subQ10])]});var subQ12=sQuery(id+"F0.wireOp",EDGE,"E0.left");var subQ15=sQuery(id+"F0.wireOp",EDGE,"E0.right");var subQ21=sQuery(id+"F0.wireOp",EDGE,"E0.top");var subQ23=sQuery(id+"F0.wireOp",EDGE,"E1.left");var subQ25=sQuery(id+"F0.wireOp",EDGE,"E1.bottom");var subQ26=sQuery(id+"F0.wireOp",EDGE,"E1.top");var subQ27=sQuery(id+"F0.wireOp",EDGE,"E1.right");var subQ28=makeQuery(id+"F1.opExtrude","CAP_FACE",FACE,{"disambiguationData":[OSD([subQ10,subQ21,subQ12,subQ15,subQ25,subQ26,subQ23,subQ27])],"isStart":false});Q0=makeQuery(id+"F23.boolean.opBoolean","SPLIT",FACE,{"disambiguationData":[TD([subQ11])],"derivedFrom":makeQuery(id+"F21.boolean.opBoolean","SPLIT",FACE,{"disambiguationData":[TD([subQ11])],"derivedFrom":makeQuery(id+"F19.boolean.opBoolean","SPLIT",FACE,{"disambiguationData":[TD([subQ11])],"derivedFrom":makeQuery(id+"F17.boolean.opBoolean","SPLIT",FACE,{"disambiguationData":[TD([subQ11])],"derivedFrom":makeQuery(id+"F15.boolean.opBoolean","SPLIT",FACE,{"disambiguationData":[TD([subQ11])],"derivedFrom":makeQuery(id+"F13.boolean.opBoolean","SPLIT",FACE,{"disambiguationData":[TD([subQ11])],"derivedFrom":makeQuery(id+"F11.boolean.opBoolean","SPLIT",FACE,{"disambiguationData":[TD([subQ11])],"derivedFrom":makeQuery(id+"F9.boolean.opBoolean","SPLIT",FACE,{"disambiguationData":[TD([subQ11])],"derivedFrom":makeQuery(id+"F7.boolean.opBoolean","SPLIT",FACE,{"disambiguationData":[TD([subQ11])],"derivedFrom":makeQuery(id+"F5.boolean.opBoolean","SPLIT",FACE,{"disambiguationData":[TD([subQ11])],"derivedFrom":subQ28})})})})})})})})})});}
            var sketch = newSketch(context, id + "F24", { "sketchPlane" : qUnion([Q0])});
            skPoint(sketch, "E101", {"position": v(0, -40) * mm});
            skCircle(sketch, "E102", {"center": v(0, -40) * mm, "radius": 5 * mm});
            skLineSegment(sketch, "E103", {"start": v(-50, -40) * mm, "end": v(50, -39.64) * mm});
            skLineSegment(sketch, "E104", {"start": v(-50, -38.5) * mm, "end": v(50, -38.14) * mm});
            skLineSegment(sketch, "E105", {"start": v(-50, -41.5) * mm, "end": v(50, -41.14) * mm});
            skSolve(sketch);
        }
        {
            var Q0;
            {var subQ0=sQuery(id+"F24.wireOp",EDGE,"E102");var subQ1=sQuery(id+"F2.wireOp",EDGE,"E9");var subQ2=makeQuery(id+"F3.boolean.opBoolean","COPY",EDGE,{"derivedFrom":makeQuery(id+"F3.opExtrude","CAP_EDGE",EDGE,{"disambiguationData":[OSD([subQ1])],"isStart":true})});var subQ3=makeQuery(id+"F24.imprint","INTERSECT",VERTEX,{"derivedFrom":[subQ2,subQ0]});Q0=makeQuery(id+"F24.imprint","IMPRINT",FACE,{"disambiguationData":[TD([[makeQuery(id+"F24.imprint","IMPRINT",EDGE,{"disambiguationData":[TD([[subQ3,-1.0]])],"derivedFrom":subQ0}),-1.0]])]});}
            var Q1;
            {var subQ0=sQuery(id+"F24.wireOp",EDGE,"E103");var subQ1=sQuery(id+"F24.wireOp",EDGE,"E102");var subQ2=makeQuery(id+"F24.imprint","INTERSECT",VERTEX,{"disambiguationData":[OD(1.0)],"derivedFrom":[subQ1,subQ0]});Q1=makeQuery(id+"F24.imprint","IMPRINT",FACE,{"disambiguationData":[TD([[makeQuery(id+"F24.imprint","IMPRINT",EDGE,{"disambiguationData":[TD([[subQ2,-1.0]])],"derivedFrom":subQ1}),-1.0]])]});}
            var Q2;
            {var subQ0=sQuery(id+"F24.wireOp",EDGE,"E102");var subQ6=makeQuery(id+"F24.imprint","INTERSECT",VERTEX,{"derivedFrom":[makeQuery(id+"F23.boolean.opBoolean","COPY",EDGE,{"derivedFrom":makeQuery(id+"F23.opExtrude","CAP_EDGE",EDGE,{"disambiguationData":[OSD([sQuery(id+"F22.wireOp",EDGE,"E99")])],"isStart":true})}),subQ0]});Q2=makeQuery(id+"F24.imprint","IMPRINT",FACE,{"disambiguationData":[TD([[makeQuery(id+"F24.imprint","IMPRINT",EDGE,{"disambiguationData":[TD([[subQ6,1.0]])],"derivedFrom":subQ0}),1.0]])]});}
            var Q3;
            {var subQ0=sQuery(id+"F24.wireOp",EDGE,"E103");var subQ1=sQuery(id+"F24.wireOp",EDGE,"E102");var subQ2=makeQuery(id+"F24.imprint","INTERSECT",VERTEX,{"disambiguationData":[OD(1.0)],"derivedFrom":[subQ1,subQ0]});Q3=makeQuery(id+"F24.imprint","IMPRINT",FACE,{"disambiguationData":[TD([[makeQuery(id+"F24.imprint","IMPRINT",EDGE,{"disambiguationData":[TD([[subQ2,-1.0]])],"derivedFrom":subQ1}),1.0]])]});}
            var Q4;
            {var subQ0=sQuery(id+"F24.wireOp",EDGE,"E102");var subQ1=sQuery(id+"F22.wireOp",EDGE,"E99");var subQ2=makeQuery(id+"F23.boolean.opBoolean","COPY",EDGE,{"derivedFrom":makeQuery(id+"F23.opExtrude","CAP_EDGE",EDGE,{"disambiguationData":[OSD([subQ1])],"isStart":true})});var subQ3=makeQuery(id+"F24.imprint","INTERSECT",VERTEX,{"derivedFrom":[subQ2,subQ0]});Q4=makeQuery(id+"F24.imprint","IMPRINT",FACE,{"disambiguationData":[TD([[makeQuery(id+"F24.imprint","IMPRINT",EDGE,{"disambiguationData":[TD([[subQ3,1.0]])],"derivedFrom":subQ0}),-1.0]])]});}
            var Q5;
            {var subQ0=sQuery(id+"F24.wireOp",EDGE,"E103");var subQ1=sQuery(id+"F24.wireOp",EDGE,"E102");var subQ2=makeQuery(id+"F24.imprint","INTERSECT",VERTEX,{"disambiguationData":[OD(0.0)],"derivedFrom":[subQ1,subQ0]});Q5=makeQuery(id+"F24.imprint","IMPRINT",FACE,{"disambiguationData":[TD([[makeQuery(id+"F24.imprint","IMPRINT",EDGE,{"disambiguationData":[TD([[subQ2,1.0]])],"derivedFrom":subQ1}),-1.0]])]});}
            var Q6;
            {var subQ0=sQuery(id+"F24.wireOp",EDGE,"E102");var subQ1=makeQuery(id+"F3.boolean.opBoolean","COPY",EDGE,{"derivedFrom":makeQuery(id+"F3.opExtrude","CAP_EDGE",EDGE,{"disambiguationData":[OSD([sQuery(id+"F2.wireOp",EDGE,"E9")])],"isStart":true})});var subQ2=makeQuery(id+"F24.imprint","INTERSECT",VERTEX,{"derivedFrom":[subQ1,subQ0]});Q6=makeQuery(id+"F24.imprint","IMPRINT",FACE,{"disambiguationData":[TD([[makeQuery(id+"F24.imprint","IMPRINT",EDGE,{"disambiguationData":[TD([[subQ2,1.0]])],"derivedFrom":subQ0}),-1.0]])]});}
            var Q7;
            {var subQ0=sQuery(id+"F24.wireOp",EDGE,"E102");var subQ1=makeQuery(id+"F23.boolean.opBoolean","COPY",EDGE,{"derivedFrom":makeQuery(id+"F23.opExtrude","CAP_EDGE",EDGE,{"disambiguationData":[OSD([sQuery(id+"F22.wireOp",EDGE,"E99")])],"isStart":true})});var subQ2=makeQuery(id+"F24.imprint","INTERSECT",VERTEX,{"derivedFrom":[subQ1,subQ0]});Q7=makeQuery(id+"F24.imprint","IMPRINT",FACE,{"disambiguationData":[TD([[makeQuery(id+"F24.imprint","IMPRINT",EDGE,{"disambiguationData":[TD([[subQ2,-1.0]])],"derivedFrom":subQ0}),-1.0]])]});}
            extrude(context, id + "F25", {"entities" : qUnion([Q0, Q1, Q2, Q3, Q4, Q5, Q6, Q7]), "operationType" : NewBodyOperationType.REMOVE, "oppositeDirection" : true, "depth" : 2 * mm});
        }
        {
            var Q0;
            {var subQ0=sQuery(id+"F0.wireOp",EDGE,"E0.bottom");var subQ1=makeQuery(id+"F1.opExtrude","SWEPT_FACE",FACE,{"disambiguationData":[OSD([subQ0])]});var subQ2=sQuery(id+"F0.wireOp",EDGE,"E0.right");var subQ4=sQuery(id+"F0.wireOp",EDGE,"E0.left");var subQ21=sQuery(id+"F0.wireOp",EDGE,"E0.top");var subQ23=sQuery(id+"F0.wireOp",EDGE,"E1.left");var subQ25=sQuery(id+"F0.wireOp",EDGE,"E1.bottom");var subQ26=sQuery(id+"F0.wireOp",EDGE,"E1.top");var subQ27=sQuery(id+"F0.wireOp",EDGE,"E1.right");var subQ28=makeQuery(id+"F1.opExtrude","CAP_FACE",FACE,{"disambiguationData":[OSD([subQ0,subQ21,subQ4,subQ2,subQ25,subQ26,subQ23,subQ27])],"isStart":false});Q0=makeQuery(id+"F25.boolean.opBoolean","SPLIT",FACE,{"disambiguationData":[TD([subQ1])],"derivedFrom":makeQuery(id+"F23.boolean.opBoolean","SPLIT",FACE,{"disambiguationData":[TD([subQ1])],"derivedFrom":makeQuery(id+"F21.boolean.opBoolean","SPLIT",FACE,{"disambiguationData":[TD([subQ1])],"derivedFrom":makeQuery(id+"F19.boolean.opBoolean","SPLIT",FACE,{"disambiguationData":[TD([subQ1])],"derivedFrom":makeQuery(id+"F17.boolean.opBoolean","SPLIT",FACE,{"disambiguationData":[TD([subQ1])],"derivedFrom":makeQuery(id+"F15.boolean.opBoolean","SPLIT",FACE,{"disambiguationData":[TD([subQ1])],"derivedFrom":makeQuery(id+"F13.boolean.opBoolean","SPLIT",FACE,{"disambiguationData":[TD([subQ1])],"derivedFrom":makeQuery(id+"F11.boolean.opBoolean","SPLIT",FACE,{"disambiguationData":[TD([subQ1])],"derivedFrom":makeQuery(id+"F9.boolean.opBoolean","SPLIT",FACE,{"disambiguationData":[TD([subQ1])],"derivedFrom":makeQuery(id+"F7.boolean.opBoolean","SPLIT",FACE,{"disambiguationData":[TD([subQ1])],"derivedFrom":makeQuery(id+"F5.boolean.opBoolean","SPLIT",FACE,{"disambiguationData":[TD([subQ1])],"derivedFrom":subQ28})})})})})})})})})})});}
            var sketch = newSketch(context, id + "F26", { "sketchPlane" : qUnion([Q0])});
            skText(sketch, "E106", { "text": "S", "fontName": "OpenSans-Regular.ttf"});
            const initialGuessF26  = {"E106": [-0.002, -0.0495, 1, 0, 0.00764]};
            skSetInitialGuess(sketch, initialGuessF26);
            skSolve(sketch);
        }
        {
            var Q0;
            Q0 = qSketchRegion(id + "F26", true);
            extrude(context, id + "F27", {"entities" : qUnion([Q0]), "operationType" : NewBodyOperationType.ADD, "depth" : 1.5 * mm});
        }
    });
